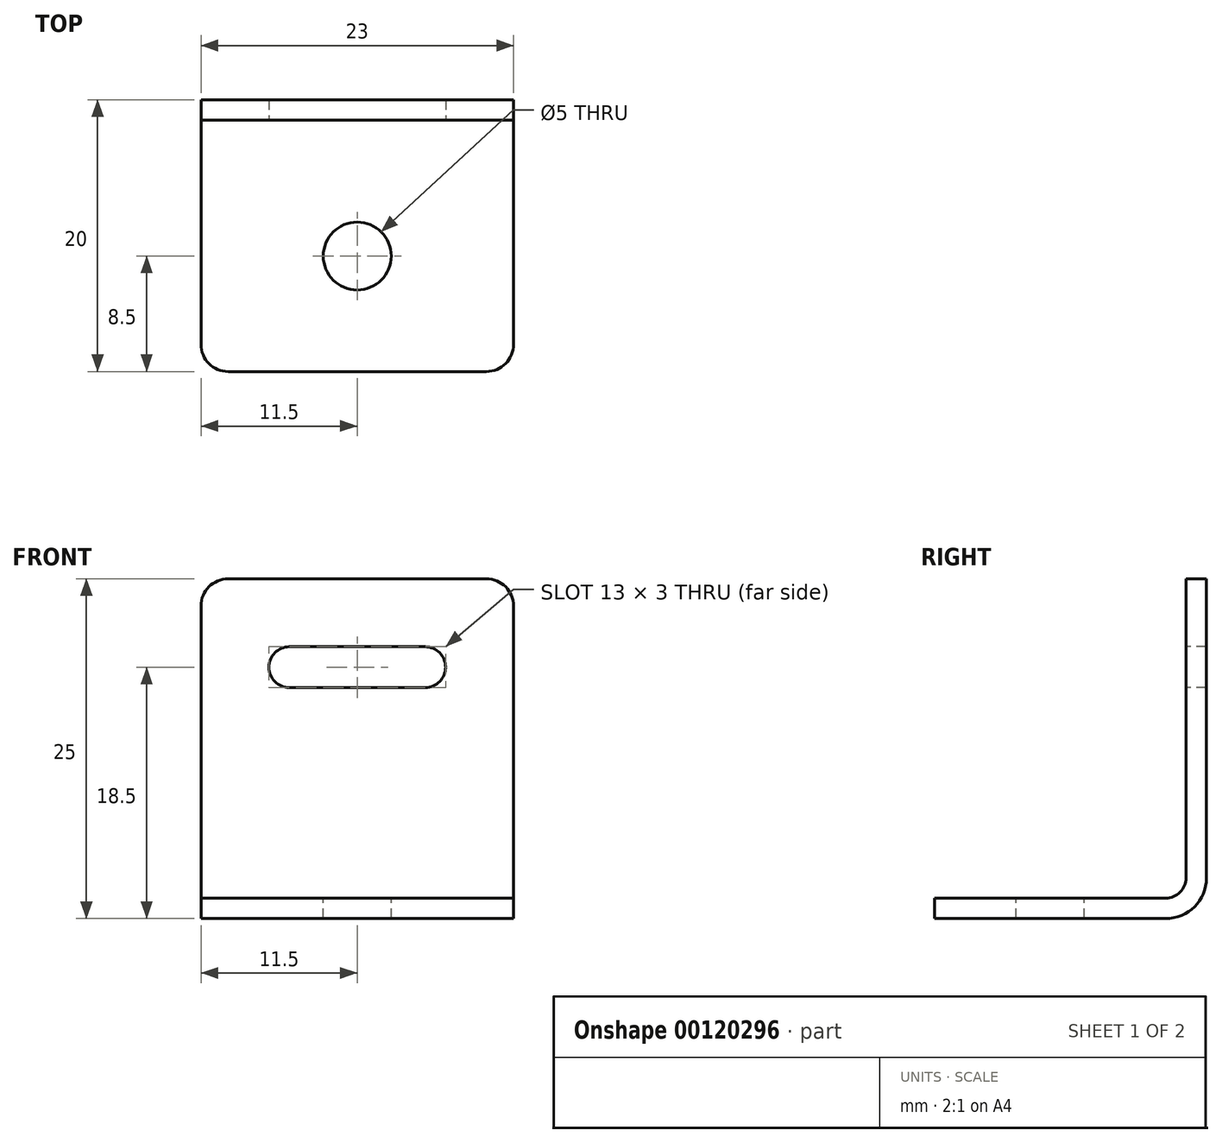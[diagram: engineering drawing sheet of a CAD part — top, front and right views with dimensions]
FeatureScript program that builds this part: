
annotation { "Feature Type Name" : "Feature", "Feature Type Description" : "" }
export const myFeature = defineFeature(function(context is Context, id is Id, definition is map)
    precondition{}
    {
        {
            var Q0;
            Q0=qCreatedBy(makeId("Right.planeOp"),FACE);
            var sketch = newSketch(context, id + "F0", { "sketchPlane" : qUnion([Q0])});
            skLineSegment(sketch, "E0", {"start": v(0, 3) * mm, "end": v(0, 25) * mm});
            skLineSegment(sketch, "E1", {"start": v(0, 25) * mm, "end": v(-1.5, 25) * mm});
            skLineSegment(sketch, "E2", {"start": v(-1.5, 25) * mm, "end": v(-1.5, 3) * mm});
            skLineSegment(sketch, "E3", {"start": v(-3, 1.5) * mm, "end": v(-20, 1.5) * mm});
            skLineSegment(sketch, "E4", {"start": v(-20, 1.5) * mm, "end": v(-20, 0) * mm});
            skLineSegment(sketch, "E5", {"start": v(-20, 0) * mm, "end": v(-3, 0) * mm});
            skPoint(sketch, "E6.visualSharp", {"position": v(0, 0) * mm});
            skArc(sketch, "E6.filletArc", {"start": v(-3, 0) * mm, "mid": v(-0.88, 0.88) * mm, "end": v(0, 3) * mm});
            skPoint(sketch, "E7.visualSharp", {"position": v(-1.5, 1.5) * mm});
            skArc(sketch, "E7.filletArc", {"start": v(-3, 1.5) * mm, "mid": v(-1.94, 1.94) * mm, "end": v(-1.5, 3) * mm});
            skSolve(sketch);
        }
        {
            var Q0;
            Q0 = qSketchRegion(id + "F0", true);
            extrude(context, id + "F1", {"entities" : qUnion([Q0]), "endBound" : BoundingType.SYMMETRIC, "depth" : 23 * mm});
        }
        {
            var Q0;
            Q0=makeQuery(id+"F1.opExtrude","SWEPT_FACE",FACE,{"disambiguationData":[OSD([sQuery(id+"F0.wireOp",EDGE,"E3")])]});
            var sketch = newSketch(context, id + "F2", { "sketchPlane" : qUnion([Q0])});
            skLineSegment(sketch, "E8", {"start": v(-11.5, -20) * mm, "end": v(11.5, -3) * mm, "construction": true});
            skLineSegment(sketch, "E9", {"start": v(-11.5, -3) * mm, "end": v(11.5, -20) * mm, "construction": true});
            skCircle(sketch, "E10", {"center": v(0, -11.5) * mm, "radius": 2.5 * mm});
            skSolve(sketch);
        }
        {
            var Q0;
            Q0 = qSketchRegion(id + "F2", true);
            extrude(context, id + "F3", {"entities" : qUnion([Q0]), "operationType" : NewBodyOperationType.REMOVE, "oppositeDirection" : true, "depth" : 25 * mm});
        }
        {
            var Q0;
            Q0=makeQuery(id+"F1.opExtrude","SWEPT_FACE",FACE,{"disambiguationData":[OSD([sQuery(id+"F0.wireOp",EDGE,"E2")])]});
            var sketch = newSketch(context, id + "F4", { "sketchPlane" : qUnion([Q0])});
            skLineSegment(sketch, "E11", {"start": v(0, 3) * mm, "end": v(0, 25) * mm, "construction": true});
            skLineSegment(sketch, "E12.bottom", {"start": v(-5, 20) * mm, "end": v(5, 20) * mm});
            skLineSegment(sketch, "E12.top", {"start": v(-5, 17) * mm, "end": v(5, 17) * mm});
            skPoint(sketch, "E12.middle", {"position": v(0, 18.5) * mm});
            skArc(sketch, "E13", {"start": v(-5, 20) * mm, "mid": v(-6.5, 18.5) * mm, "end": v(-5, 17) * mm});
            skArc(sketch, "E14", {"start": v(5, 17) * mm, "mid": v(6.5, 18.5) * mm, "end": v(5, 20) * mm});
            skSolve(sketch);
        }
        {
            var Q0;
            Q0=makeQuery(id+"F4.imprint","IMPRINT",FACE,{"disambiguationData":[TD([[makeQuery(id+"F4.imprint","IMPRINT",EDGE,{"derivedFrom":sQuery(id+"F4.wireOp",EDGE,"E12.bottom")}),-1.0]])]});
            extrude(context, id + "F5", {"entities" : qUnion([Q0]), "operationType" : NewBodyOperationType.REMOVE, "oppositeDirection" : true, "depth" : 25 * mm});
        }
        {
            var Q0;
            Q0=makeQuery(id+"F1.opExtrude","CAP_EDGE",EDGE,{"disambiguationData":[OSD([sQuery(id+"F0.wireOp",EDGE,"E1")])],"isStart":false});
            var Q1;
            Q1=makeQuery(id+"F1.opExtrude","CAP_EDGE",EDGE,{"disambiguationData":[OSD([sQuery(id+"F0.wireOp",EDGE,"E1")])],"isStart":true});
            var Q2;
            Q2=makeQuery(id+"F1.opExtrude","CAP_EDGE",EDGE,{"disambiguationData":[OSD([sQuery(id+"F0.wireOp",EDGE,"E4")])],"isStart":false});
            var Q3;
            Q3=makeQuery(id+"F1.opExtrude","CAP_EDGE",EDGE,{"disambiguationData":[OSD([sQuery(id+"F0.wireOp",EDGE,"E4")])],"isStart":true});
            fillet(context, id + "F6", {"entities" : qUnion([Q0, Q1, Q2, Q3]), "radius" : 2 * mm, "tangentPropagation" : true, "allowEdgeOverflow" : false});
        }
    });
